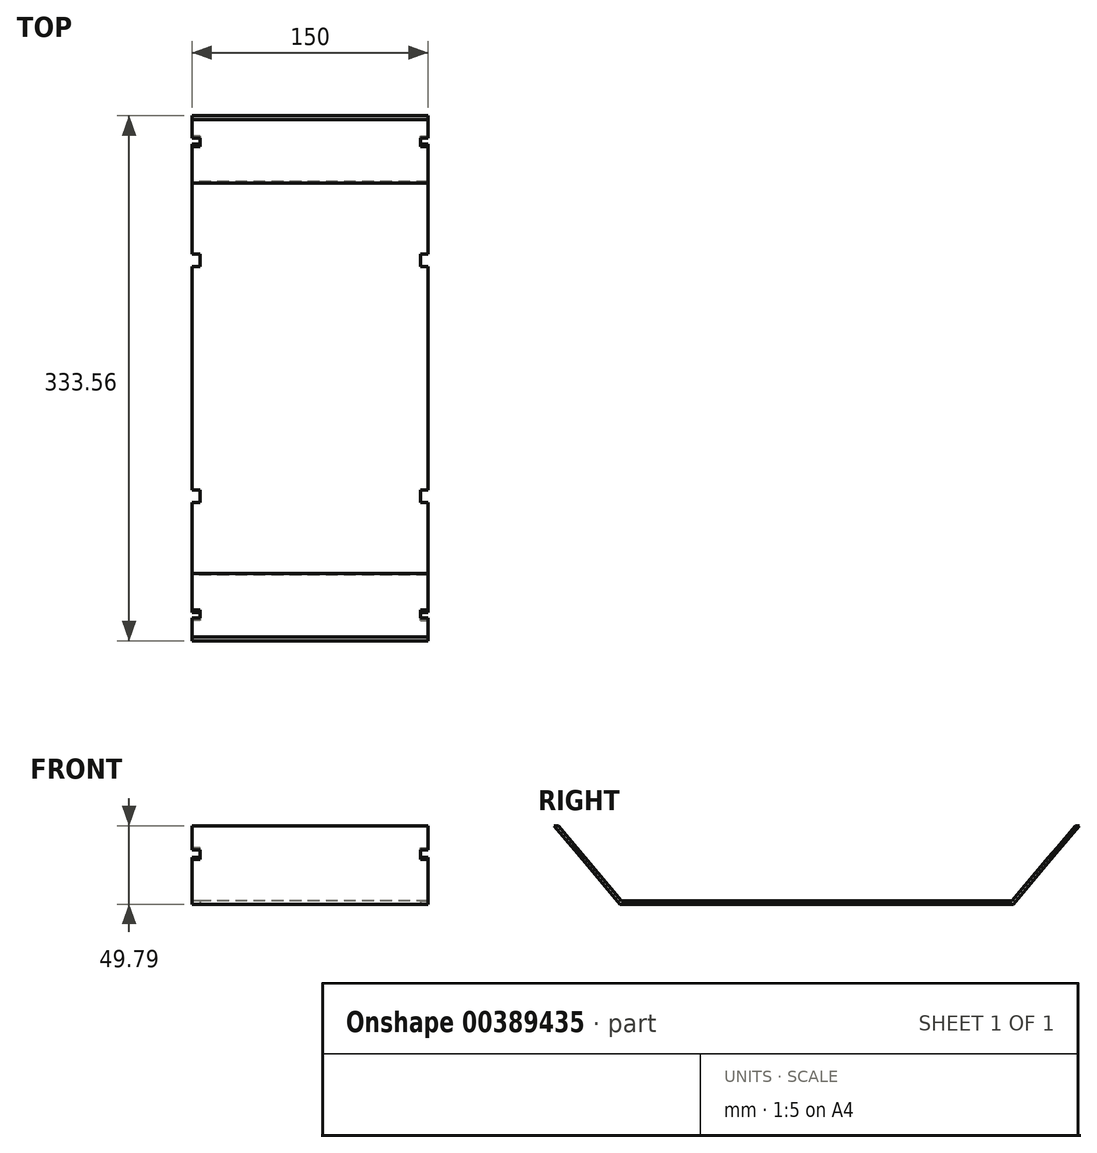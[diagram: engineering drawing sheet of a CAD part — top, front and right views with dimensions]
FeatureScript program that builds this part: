
annotation { "Feature Type Name" : "Feature", "Feature Type Description" : "" }
export const myFeature = defineFeature(function(context is Context, id is Id, definition is map)
    precondition{}
    {
        {
            var Q0;
            Q0=qCreatedBy(makeId("Right.planeOp"),FACE);
            var sketch = newSketch(context, id + "F0", { "sketchPlane" : qUnion([Q0])});
            skLineSegment(sketch, "E0", {"start": v(-125.6, 0) * mm, "end": v(124.4, 0) * mm});
            skLineSegment(sketch, "E1", {"start": v(124.4, 0) * mm, "end": v(166.19, 49.8) * mm});
            skLineSegment(sketch, "E2", {"start": v(-125.6, 0) * mm, "end": v(-167.37, 49.8) * mm});
            skLineSegment(sketch, "E3.0", {"start": v(-124.66, 2) * mm, "end": v(-164.76, 49.8) * mm});
            skLineSegment(sketch, "E3.1", {"start": v(-124.66, 2) * mm, "end": v(123.47, 2) * mm});
            skLineSegment(sketch, "E3.2", {"start": v(123.47, 2) * mm, "end": v(163.58, 49.8) * mm});
            skLineSegment(sketch, "E4", {"start": v(166.23, 49.8) * mm, "end": v(163.58, 49.8) * mm});
            skLineSegment(sketch, "E5", {"start": v(-167.37, 49.8) * mm, "end": v(-164.76, 49.8) * mm});
            skSolve(sketch);
        }
        {
            var Q0;
            Q0=qSketchRegion(id+"F0",true);
            extrude(context, id + "F1", {"entities" : qUnion([Q0]), "endBound" : BoundingType.SYMMETRIC, "depth" : 150 * mm});
        }
        {
            var Q0;
            Q0=makeQuery(id+"F1.opExtrude","CAP_FACE",FACE,{"disambiguationData":[OSD([sQuery(id+"F0.wireOp",EDGE,"E0"),sQuery(id+"F0.wireOp",EDGE,"E1"),sQuery(id+"F0.wireOp",EDGE,"E2"),sQuery(id+"F0.wireOp",EDGE,"E3.0"),sQuery(id+"F0.wireOp",EDGE,"E3.1"),sQuery(id+"F0.wireOp",EDGE,"E3.2"),sQuery(id+"F0.wireOp",EDGE,"E4"),sQuery(id+"F0.wireOp",EDGE,"E5")])],"isStart":false});
            var sketch = newSketch(context, id + "F2", { "sketchPlane" : qUnion([Q0])});
            skLineSegment(sketch, "E6.bottom", {"start": v(-79.6, 2) * mm, "end": v(-71.6, 2) * mm});
            skLineSegment(sketch, "E6.top", {"start": v(-79.6, 0) * mm, "end": v(-71.6, 0) * mm});
            skLineSegment(sketch, "E6.left", {"start": v(-79.6, 2) * mm, "end": v(-79.6, 0) * mm});
            skLineSegment(sketch, "E6.right", {"start": v(-71.6, 2) * mm, "end": v(-71.6, 0) * mm});
            skLineSegment(sketch, "E7.bottom", {"start": v(70.4, 2) * mm, "end": v(78.4, 2) * mm});
            skLineSegment(sketch, "E7.top", {"start": v(70.4, 0) * mm, "end": v(78.4, 0) * mm});
            skLineSegment(sketch, "E7.left", {"start": v(70.4, 2) * mm, "end": v(70.4, 0) * mm});
            skLineSegment(sketch, "E7.right", {"start": v(78.4, 2) * mm, "end": v(78.4, 0) * mm});
            skLineSegment(sketch, "E8", {"start": v(-154.52, 34.47) * mm, "end": v(-152.99, 35.76) * mm});
            skLineSegment(sketch, "E9", {"start": v(-149.38, 28.34) * mm, "end": v(-147.84, 29.63) * mm});
            skLineSegment(sketch, "E10", {"start": v(153.33, 34.47) * mm, "end": v(151.8, 35.76) * mm});
            skLineSegment(sketch, "E11", {"start": v(148.19, 28.34) * mm, "end": v(146.66, 29.63) * mm});
            skSolve(sketch);
        }
        {
            var Q0;
            Q0 = qSketchRegion(id + "F2", true);
            var Q1;
            {var subQ0=sQuery(id+"F2.wireOp",EDGE,"E10");Q1=makeQuery(id+"F2.imprint","IMPRINT",FACE,{"disambiguationData":[TD([[makeQuery(id+"F2.imprint","IMPRINT",EDGE,{"derivedFrom":subQ0}),1.0]])]});}
            var Q2;
            {var subQ0=sQuery(id+"F2.wireOp",EDGE,"E8");Q2=makeQuery(id+"F2.imprint","IMPRINT",FACE,{"disambiguationData":[TD([[makeQuery(id+"F2.imprint","IMPRINT",EDGE,{"derivedFrom":subQ0}),-1.0]])]});}
            extrude(context, id + "F3", {"entities" : qUnion([Q0, Q1, Q2]), "operationType" : NewBodyOperationType.REMOVE, "oppositeDirection" : true, "depth" : 5 * mm});
        }
        {
            var Q0;
            Q0=makeQuery(id+"F1.opExtrude","SWEPT_BODY",BODY,{"disambiguationData":[OSD([sQuery(id+"F0.wireOp",EDGE,"E0"),sQuery(id+"F0.wireOp",EDGE,"E1"),sQuery(id+"F0.wireOp",EDGE,"E2"),sQuery(id+"F0.wireOp",EDGE,"E3.0"),sQuery(id+"F0.wireOp",EDGE,"E3.1"),sQuery(id+"F0.wireOp",EDGE,"E3.2"),sQuery(id+"F0.wireOp",EDGE,"E4"),sQuery(id+"F0.wireOp",EDGE,"E5")])]});
            var Q1;
            Q1=qCreatedBy(makeId("Right.planeOp"),FACE);
            mirror(context, id + "F4", {"operationType" : NewBodyOperationType.INTERSECT, "entities" : qUnion([Q0]), "mirrorPlane" : qUnion([Q1])});
        }
    });
